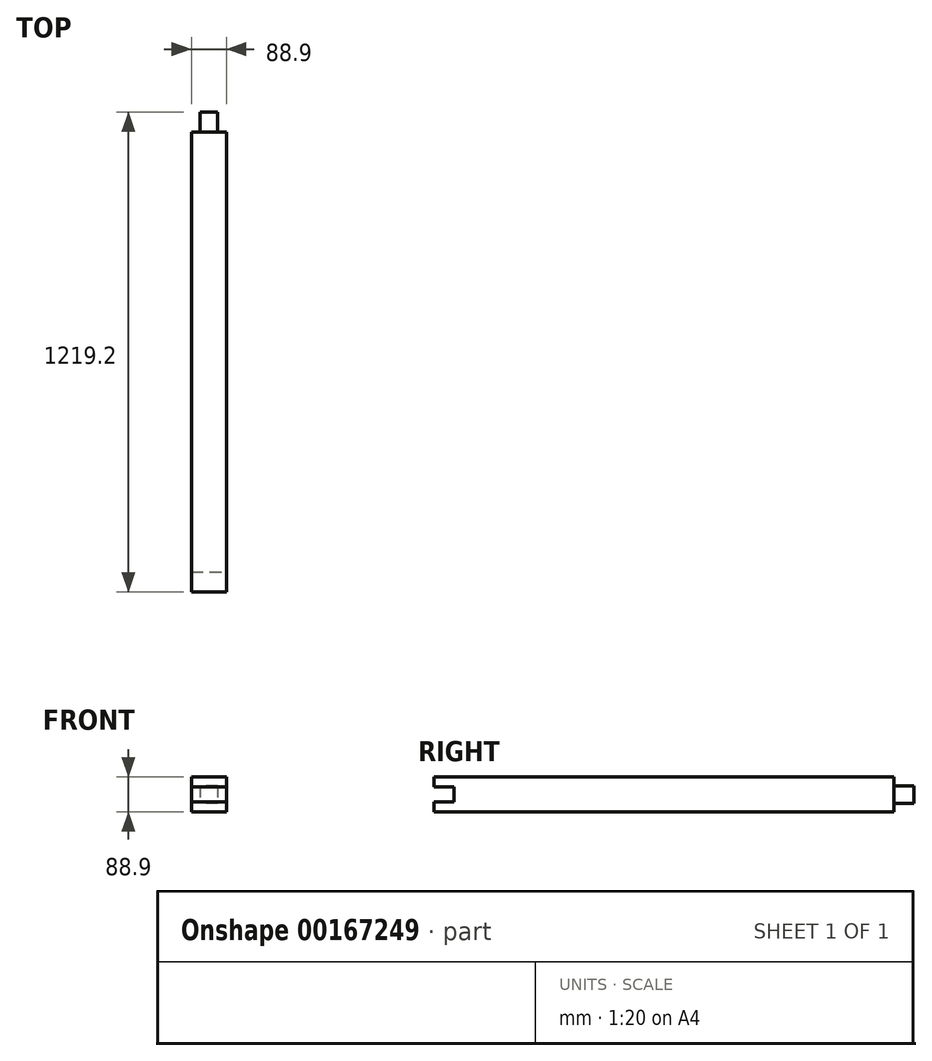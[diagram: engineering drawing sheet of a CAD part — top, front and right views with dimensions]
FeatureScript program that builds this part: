
annotation { "Feature Type Name" : "Feature", "Feature Type Description" : "" }
export const myFeature = defineFeature(function(context is Context, id is Id, definition is map)
    precondition{}
    {
        {
            var Q0;
            Q0=qCreatedBy(makeId("Front.planeOp"),FACE);
            var sketch = newSketch(context, id + "F0", { "sketchPlane" : qUnion([Q0])});
            skLineSegment(sketch, "E0.bottom", {"start": v(0, 0) * mm, "end": v(88.9, 0) * mm});
            skLineSegment(sketch, "E0.top", {"start": v(0, 88.9) * mm, "end": v(88.9, 88.9) * mm});
            skLineSegment(sketch, "E0.left", {"start": v(0, 0) * mm, "end": v(0, 88.9) * mm});
            skLineSegment(sketch, "E0.right", {"start": v(88.9, 0) * mm, "end": v(88.9, 88.9) * mm});
            skSolve(sketch);
        }
        {
            var Q0;
            Q0=makeQuery(id+"F0.imprint","IMPRINT",FACE,{"disambiguationData":[TD([[makeQuery(id+"F0.imprint","IMPRINT",EDGE,{"derivedFrom":sQuery(id+"F0.wireOp",EDGE,"E0.bottom")}),1.0]])]});
            extrude(context, id + "F1", {"entities" : qUnion([Q0]), "depth" : 1219.2 * mm});
        }
        {
            var Q0;
            Q0=makeQuery(id+"F1.opExtrude","SWEPT_FACE",FACE,{"disambiguationData":[OSD([sQuery(id+"F0.wireOp",EDGE,"E0.right")])]});
            var sketch = newSketch(context, id + "F2", { "sketchPlane" : qUnion([Q0])});
            skLineSegment(sketch, "E1", {"start": v(-1219.2, 63.5) * mm, "end": v(-1168.4, 63.5) * mm});
            skLineSegment(sketch, "E2", {"start": v(-1168.4, 63.5) * mm, "end": v(-1168.4, 25.4) * mm});
            skLineSegment(sketch, "E3", {"start": v(-1168.4, 25.4) * mm, "end": v(-1219.2, 25.4) * mm});
            skLineSegment(sketch, "E4", {"start": v(-1219.2, 25.4) * mm, "end": v(-1219.2, 63.5) * mm});
            skLineSegment(sketch, "E5", {"start": v(-1168.4, 63.5) * mm, "end": v(-1168.4, 88.9) * mm, "construction": true});
            skLineSegment(sketch, "E6", {"start": v(-1168.4, 25.4) * mm, "end": v(-1168.4, 0) * mm, "construction": true});
            skSolve(sketch);
        }
        {
            var Q0;
            Q0=makeQuery(id+"F2.imprint","IMPRINT",FACE,{"disambiguationData":[TD([[makeQuery(id+"F2.imprint","IMPRINT",EDGE,{"derivedFrom":sQuery(id+"F2.wireOp",EDGE,"E1")}),-1.0]])]});
            extrude(context, id + "F3", {"entities" : qUnion([Q0]), "operationType" : NewBodyOperationType.REMOVE, "oppositeDirection" : true, "depth" : 101.6 * mm});
        }
        {
            var Q0;
            Q0=makeQuery(id+"F1.opExtrude","CAP_FACE",FACE,{"disambiguationData":[OSD([sQuery(id+"F0.wireOp",EDGE,"E0.bottom"),sQuery(id+"F0.wireOp",EDGE,"E0.top"),sQuery(id+"F0.wireOp",EDGE,"E0.left"),sQuery(id+"F0.wireOp",EDGE,"E0.right")])],"isStart":true});
            var sketch = newSketch(context, id + "F4", { "sketchPlane" : qUnion([Q0])});
            skLineSegment(sketch, "E7", {"start": v(-88.9, 88.9) * mm, "end": v(0, 0) * mm, "construction": true});
            skLineSegment(sketch, "E8", {"start": v(0, 88.9) * mm, "end": v(-88.9, 0) * mm, "construction": true});
            skLineSegment(sketch, "E9.bottom", {"start": v(-66.67, 66.68) * mm, "end": v(-22.22, 66.68) * mm});
            skLineSegment(sketch, "E9.top", {"start": v(-66.67, 22.22) * mm, "end": v(-22.22, 22.22) * mm});
            skLineSegment(sketch, "E9.left", {"start": v(-66.67, 66.68) * mm, "end": v(-66.67, 22.22) * mm});
            skLineSegment(sketch, "E9.right", {"start": v(-22.22, 66.68) * mm, "end": v(-22.22, 22.22) * mm});
            skPoint(sketch, "E9.middle", {"position": v(-44.45, 44.45) * mm});
            skSolve(sketch);
        }
        {
            var Q0;
            Q0=makeQuery(id+"F4.imprint","IMPRINT",FACE,{"disambiguationData":[TD([[makeQuery(id+"F4.imprint","IMPRINT",EDGE,{"derivedFrom":sQuery(id+"F4.wireOp",EDGE,"E9.bottom")}),1.0]])]});
            extrude(context, id + "F5", {"entities" : qUnion([Q0]), "operationType" : NewBodyOperationType.REMOVE, "oppositeDirection" : true, "depth" : 50.8 * mm});
        }
    });
